# Revit family: LIO-Suspension
name_source: partatom
category: Lighting Fixtures
units: mm (PartAtom-declared; Revit-internal decimal feet)

## family parameters
Always vertical = Yes
Cut with Voids When Loaded = No
Host = Ceiling
Light Source = No
OmniClass Number = 23.80.70.11
OmniClass Title = Luminaries for Internal Lighting
Part Type = Normal
Room Calculation Point = No
Round Connector Dimension = Use Diameter
Shared = No

## types (3) — shared parameters
Bulb Diametr = 15 mm  [stored 0.0492126 ft]
Description = SUSPENSION
Designer = Studio Debonademeo
Manufacturer = Vistosi
Manufacturer country = Italy
Model = LIO
Type Comments = Studio Debonademeo
URL = https://vistosi.com
URL Product Page = https://vistosi.it
zero-valued in all types: Default Elevation

## per-type parameters (varying)
| type | Base Type | Depth | LIO SP 1P | LIO SP 5 | LIO_Other | Lampshade Type | Width |
| LIO SP 1P | LIO_Top base : LIO | 0 mm  [stored 0 ft] | Yes | No | Yes | LIO_Lampshade : LIO LT P | 7 mm  [stored 0.0229659 ft] |
| LIO SP | LIO_Top base : LIO | 14 mm  [stored 0.0459318 ft] | No | No | Yes | LIO_Lampshade : LIO SP | 50 mm  [stored 0.164042 ft] |
| LIO SP 5 | LIO_Top base : LIO SP 5 | 0 mm  [stored 0 ft] | No | Yes | No | LIO_Lampshade : LIO SP | 8 mm  [stored 0.0262467 ft] |

note: [stored X ft] marks values corroborated as IEEE doubles in the binary element streams (Revit-internal decimal feet)

## geometry (parser evidence)
native form markers: Sweep x17
no freeform markers — native parametric forms only
